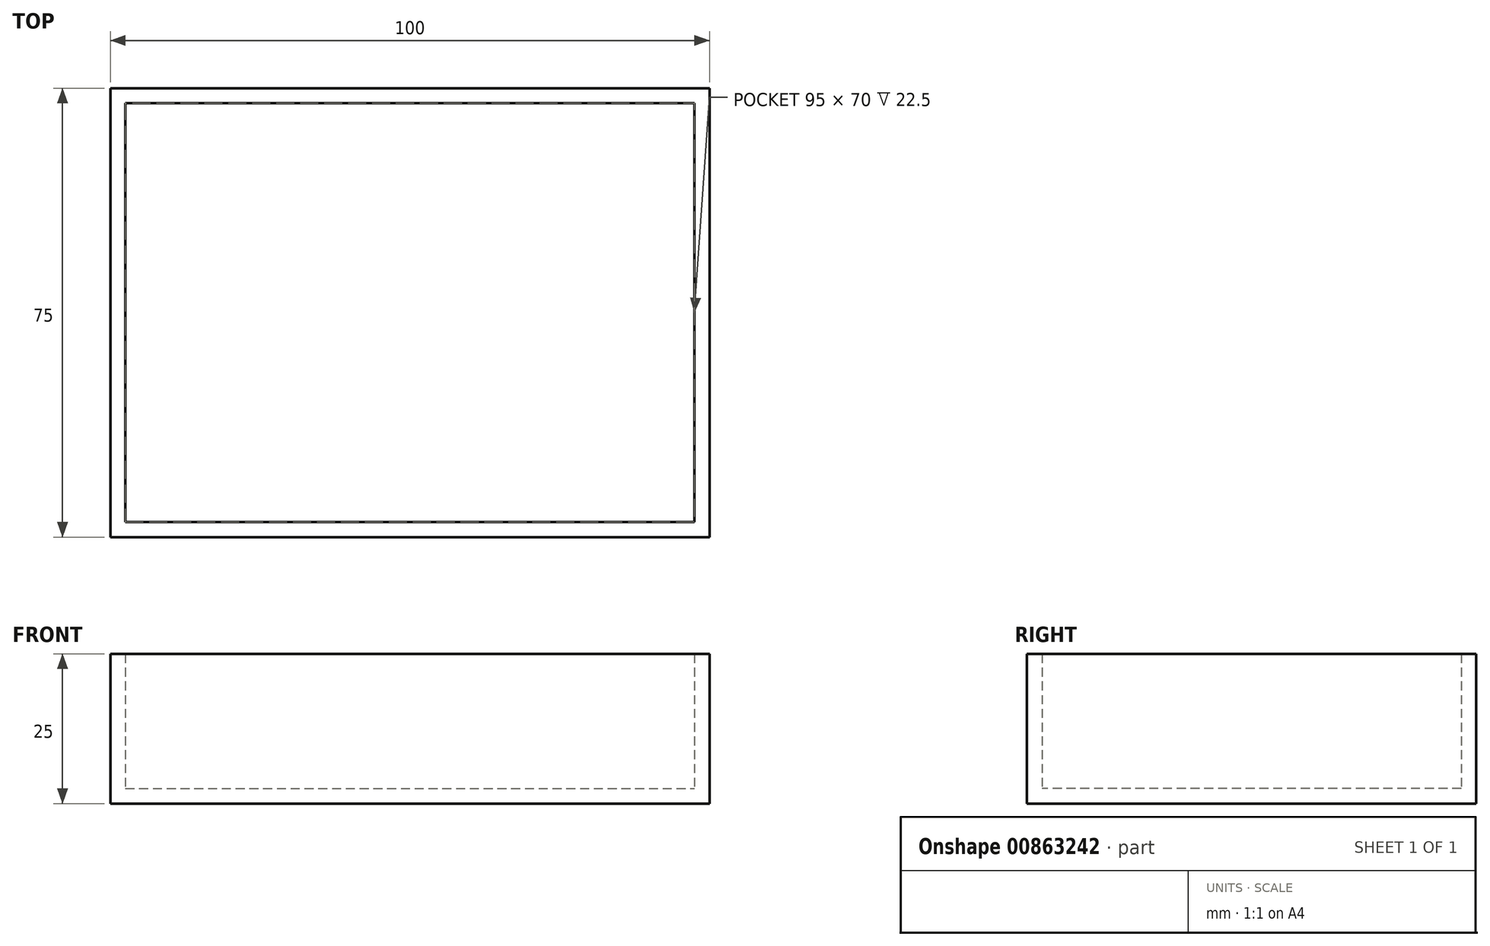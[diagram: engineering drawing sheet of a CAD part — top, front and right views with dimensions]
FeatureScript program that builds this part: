
annotation { "Feature Type Name" : "Feature", "Feature Type Description" : "" }
export const myFeature = defineFeature(function(context is Context, id is Id, definition is map)
    precondition{}
    {
        {
            var Q0;
            Q0=qCreatedBy(makeId("Top.planeOp"),FACE);
            var sketch = newSketch(context, id + "F0", { "sketchPlane" : qUnion([Q0])});
            skLineSegment(sketch, "E0.bottom", {"start": v(-50, 37.5) * mm, "end": v(50, 37.5) * mm});
            skLineSegment(sketch, "E0.top", {"start": v(-50, -37.5) * mm, "end": v(50, -37.5) * mm});
            skLineSegment(sketch, "E0.left", {"start": v(-50, 37.5) * mm, "end": v(-50, -37.5) * mm});
            skLineSegment(sketch, "E0.right", {"start": v(50, 37.5) * mm, "end": v(50, -37.5) * mm});
            skPoint(sketch, "E0.middle", {"position": v(0, 0) * mm});
            skSolve(sketch);
        }
        {
            var Q0;
            Q0 = qSketchRegion(id + "F0", true);
            extrude(context, id + "F1", {"entities" : qUnion([Q0]), "depth" : 25 * mm, "offsetDistance" : 25 * mm});
        }
        {
            var Q0;
            Q0=makeQuery(id+"F1.opExtrude","CAP_FACE",FACE,{"disambiguationData":[OSD([sQuery(id+"F0.wireOp",EDGE,"E0.bottom"),sQuery(id+"F0.wireOp",EDGE,"E0.top"),sQuery(id+"F0.wireOp",EDGE,"E0.left"),sQuery(id+"F0.wireOp",EDGE,"E0.right")])],"isStart":false});
            var Q1;
            Q1=makeQuery(id+"F1.opExtrude","SWEPT_BODY",BODY,{"disambiguationData":[OSD([sQuery(id+"F0.wireOp",EDGE,"E0.bottom"),sQuery(id+"F0.wireOp",EDGE,"E0.top"),sQuery(id+"F0.wireOp",EDGE,"E0.left"),sQuery(id+"F0.wireOp",EDGE,"E0.right")])]});
            shell(context, id + "F2", {"entities" : qUnion([Q0]), "parts" : qUnion([Q1]), "thickness" : 2.5 * mm});
        }
    });
